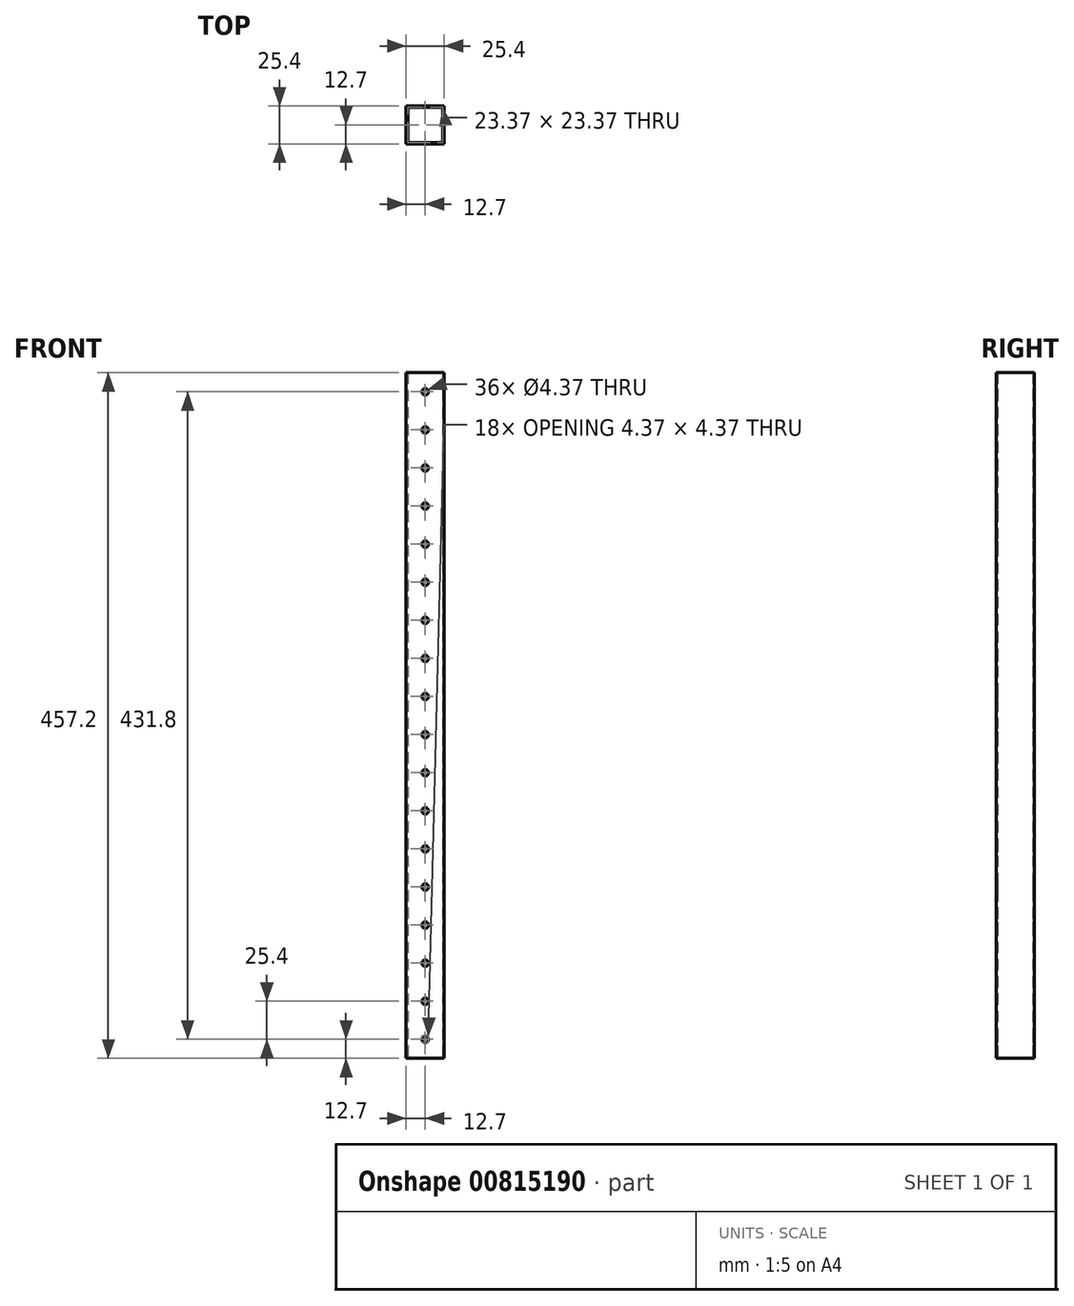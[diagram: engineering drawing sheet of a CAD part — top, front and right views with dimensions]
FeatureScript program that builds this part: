
annotation { "Feature Type Name" : "Feature", "Feature Type Description" : "" }
export const myFeature = defineFeature(function(context is Context, id is Id, definition is map)
    precondition{}
    {
        {
            var Q0;
            Q0=qCreatedBy(makeId("Top.planeOp"),FACE);
            var sketch = newSketch(context, id + "F0", { "sketchPlane" : qUnion([Q0])});
            skLineSegment(sketch, "E0.bottom", {"start": v(0, 0) * mm, "end": v(25.4, 0) * mm});
            skLineSegment(sketch, "E0.top", {"start": v(0, -25.4) * mm, "end": v(25.4, -25.4) * mm});
            skLineSegment(sketch, "E0.left", {"start": v(0, 0) * mm, "end": v(0, -25.4) * mm});
            skLineSegment(sketch, "E0.right", {"start": v(25.4, 0) * mm, "end": v(25.4, -25.4) * mm});
            skLineSegment(sketch, "E1.bottom", {"start": v(1.02, -1.02) * mm, "end": v(24.38, -1.02) * mm});
            skLineSegment(sketch, "E1.top", {"start": v(1.02, -24.38) * mm, "end": v(24.38, -24.38) * mm});
            skLineSegment(sketch, "E1.left", {"start": v(1.02, -1.02) * mm, "end": v(1.02, -24.38) * mm});
            skLineSegment(sketch, "E1.right", {"start": v(24.38, -1.02) * mm, "end": v(24.38, -24.38) * mm});
            skSolve(sketch);
        }
        {
            var Q0;
            Q0=makeQuery(id+"F0.imprint","IMPRINT",FACE,{"disambiguationData":[TD([[makeQuery(id+"F0.imprint","IMPRINT",EDGE,{"derivedFrom":sQuery(id+"F0.wireOp",EDGE,"E0.bottom")}),-1.0]])]});
            extrude(context, id + "F1", {"entities" : qUnion([Q0]), "depth" : 457.2 * mm, "offsetDistance" : 25.4 * mm});
        }
        {
            var Q0;
            Q0=makeQuery(id+"F1.opExtrude","SWEPT_FACE",FACE,{"disambiguationData":[OSD([sQuery(id+"F0.wireOp",EDGE,"E0.top")])]});
            var sketch = newSketch(context, id + "F2", { "sketchPlane" : qUnion([Q0])});
            skCircle(sketch, "E2", {"center": v(12.7, 12.7) * mm, "radius": 2.18 * mm});
            skCircle(sketch, "E3.0.1.0", {"center": v(12.7, 38.1) * mm, "radius": 2.18 * mm});
            skCircle(sketch, "E3.0.2.0", {"center": v(12.7, 63.5) * mm, "radius": 2.18 * mm});
            skCircle(sketch, "E3.0.3.0", {"center": v(12.7, 88.9) * mm, "radius": 2.18 * mm});
            skCircle(sketch, "E3.0.4.0", {"center": v(12.7, 114.3) * mm, "radius": 2.18 * mm});
            skCircle(sketch, "E3.0.5.0", {"center": v(12.7, 139.7) * mm, "radius": 2.18 * mm});
            skCircle(sketch, "E3.0.6.0", {"center": v(12.7, 165.1) * mm, "radius": 2.18 * mm});
            skCircle(sketch, "E3.0.7.0", {"center": v(12.7, 190.5) * mm, "radius": 2.18 * mm});
            skCircle(sketch, "E3.0.8.0", {"center": v(12.7, 215.9) * mm, "radius": 2.18 * mm});
            skCircle(sketch, "E3.0.9.0", {"center": v(12.7, 241.3) * mm, "radius": 2.18 * mm});
            skCircle(sketch, "E3.0.10.0", {"center": v(12.7, 266.7) * mm, "radius": 2.18 * mm});
            skCircle(sketch, "E3.0.11.0", {"center": v(12.7, 292.1) * mm, "radius": 2.18 * mm});
            skCircle(sketch, "E3.0.12.0", {"center": v(12.7, 317.5) * mm, "radius": 2.18 * mm});
            skCircle(sketch, "E3.0.13.0", {"center": v(12.7, 342.9) * mm, "radius": 2.18 * mm});
            skCircle(sketch, "E3.0.14.0", {"center": v(12.7, 368.3) * mm, "radius": 2.18 * mm});
            skCircle(sketch, "E3.0.15.0", {"center": v(12.7, 393.7) * mm, "radius": 2.18 * mm});
            skCircle(sketch, "E3.0.16.0", {"center": v(12.7, 419.1) * mm, "radius": 2.18 * mm});
            skCircle(sketch, "E3.0.17.0", {"center": v(12.7, 444.5) * mm, "radius": 2.18 * mm});
            skCircle(sketch, "E3.0.18.0", {"center": v(12.7, 469.9) * mm, "radius": 2.18 * mm});
            skCircle(sketch, "E3.0.19.0", {"center": v(12.7, 495.3) * mm, "radius": 2.18 * mm});
            skCircle(sketch, "E3.0.20.0", {"center": v(12.7, 520.7) * mm, "radius": 2.18 * mm});
            skCircle(sketch, "E3.0.21.0", {"center": v(12.7, 546.1) * mm, "radius": 2.18 * mm});
            skCircle(sketch, "E3.0.22.0", {"center": v(12.7, 571.5) * mm, "radius": 2.18 * mm});
            skCircle(sketch, "E3.0.23.0", {"center": v(12.7, 596.9) * mm, "radius": 2.18 * mm});
            skCircle(sketch, "E3.0.24.0", {"center": v(12.7, 622.3) * mm, "radius": 2.18 * mm});
            skLineSegment(sketch, "E3.direction1", {"start": v(12.7, 12.7) * mm, "end": v(38.1, 12.7) * mm, "construction": true});
            skLineSegment(sketch, "E3.direction2", {"start": v(12.7, 12.7) * mm, "end": v(12.7, 38.1) * mm, "construction": true});
            skSolve(sketch);
        }
        {
            var Q0;
            Q0=makeQuery(id+"F2.imprint","IMPRINT",FACE,{"disambiguationData":[TD([[makeQuery(id+"F2.imprint","IMPRINT",EDGE,{"derivedFrom":sQuery(id+"F2.wireOp",EDGE,"E2")}),1.0]])]});
            var Q1;
            Q1=makeQuery(id+"F2.imprint","IMPRINT",FACE,{"disambiguationData":[TD([[makeQuery(id+"F2.imprint","IMPRINT",EDGE,{"derivedFrom":sQuery(id+"F2.wireOp",EDGE,"E3.0.1.0")}),1.0]])]});
            var Q2;
            Q2=makeQuery(id+"F2.imprint","IMPRINT",FACE,{"disambiguationData":[TD([[makeQuery(id+"F2.imprint","IMPRINT",EDGE,{"derivedFrom":sQuery(id+"F2.wireOp",EDGE,"E3.0.9.0")}),1.0]])]});
            var Q3;
            Q3=makeQuery(id+"F2.imprint","IMPRINT",FACE,{"disambiguationData":[TD([[makeQuery(id+"F2.imprint","IMPRINT",EDGE,{"derivedFrom":sQuery(id+"F2.wireOp",EDGE,"E3.0.8.0")}),1.0]])]});
            var Q4;
            Q4=makeQuery(id+"F2.imprint","IMPRINT",FACE,{"disambiguationData":[TD([[makeQuery(id+"F2.imprint","IMPRINT",EDGE,{"derivedFrom":sQuery(id+"F2.wireOp",EDGE,"E3.0.7.0")}),1.0]])]});
            var Q5;
            Q5=makeQuery(id+"F2.imprint","IMPRINT",FACE,{"disambiguationData":[TD([[makeQuery(id+"F2.imprint","IMPRINT",EDGE,{"derivedFrom":sQuery(id+"F2.wireOp",EDGE,"E3.0.6.0")}),1.0]])]});
            var Q6;
            Q6=makeQuery(id+"F2.imprint","IMPRINT",FACE,{"disambiguationData":[TD([[makeQuery(id+"F2.imprint","IMPRINT",EDGE,{"derivedFrom":sQuery(id+"F2.wireOp",EDGE,"E3.0.5.0")}),1.0]])]});
            var Q7;
            Q7=makeQuery(id+"F2.imprint","IMPRINT",FACE,{"disambiguationData":[TD([[makeQuery(id+"F2.imprint","IMPRINT",EDGE,{"derivedFrom":sQuery(id+"F2.wireOp",EDGE,"E3.0.4.0")}),1.0]])]});
            var Q8;
            Q8=makeQuery(id+"F2.imprint","IMPRINT",FACE,{"disambiguationData":[TD([[makeQuery(id+"F2.imprint","IMPRINT",EDGE,{"derivedFrom":sQuery(id+"F2.wireOp",EDGE,"E3.0.3.0")}),1.0]])]});
            var Q9;
            Q9=makeQuery(id+"F2.imprint","IMPRINT",FACE,{"disambiguationData":[TD([[makeQuery(id+"F2.imprint","IMPRINT",EDGE,{"derivedFrom":sQuery(id+"F2.wireOp",EDGE,"E3.0.2.0")}),1.0]])]});
            var Q10;
            Q10=makeQuery(id+"F2.imprint","IMPRINT",FACE,{"disambiguationData":[TD([[makeQuery(id+"F2.imprint","IMPRINT",EDGE,{"derivedFrom":sQuery(id+"F2.wireOp",EDGE,"E3.0.10.0")}),1.0]])]});
            var Q11;
            Q11=makeQuery(id+"F2.imprint","IMPRINT",FACE,{"disambiguationData":[TD([[makeQuery(id+"F2.imprint","IMPRINT",EDGE,{"derivedFrom":sQuery(id+"F2.wireOp",EDGE,"E3.0.11.0")}),1.0]])]});
            var Q12;
            Q12=makeQuery(id+"F2.imprint","IMPRINT",FACE,{"disambiguationData":[TD([[makeQuery(id+"F2.imprint","IMPRINT",EDGE,{"derivedFrom":sQuery(id+"F2.wireOp",EDGE,"E3.0.12.0")}),1.0]])]});
            var Q13;
            Q13=makeQuery(id+"F2.imprint","IMPRINT",FACE,{"disambiguationData":[TD([[makeQuery(id+"F2.imprint","IMPRINT",EDGE,{"derivedFrom":sQuery(id+"F2.wireOp",EDGE,"E3.0.13.0")}),1.0]])]});
            var Q14;
            Q14=makeQuery(id+"F2.imprint","IMPRINT",FACE,{"disambiguationData":[TD([[makeQuery(id+"F2.imprint","IMPRINT",EDGE,{"derivedFrom":sQuery(id+"F2.wireOp",EDGE,"E3.0.14.0")}),1.0]])]});
            var Q15;
            Q15=makeQuery(id+"F2.imprint","IMPRINT",FACE,{"disambiguationData":[TD([[makeQuery(id+"F2.imprint","IMPRINT",EDGE,{"derivedFrom":sQuery(id+"F2.wireOp",EDGE,"E3.0.15.0")}),1.0]])]});
            var Q16;
            Q16=makeQuery(id+"F2.imprint","IMPRINT",FACE,{"disambiguationData":[TD([[makeQuery(id+"F2.imprint","IMPRINT",EDGE,{"derivedFrom":sQuery(id+"F2.wireOp",EDGE,"E3.0.16.0")}),1.0]])]});
            var Q17;
            Q17=makeQuery(id+"F2.imprint","IMPRINT",FACE,{"disambiguationData":[TD([[makeQuery(id+"F2.imprint","IMPRINT",EDGE,{"derivedFrom":sQuery(id+"F2.wireOp",EDGE,"E3.0.17.0")}),1.0]])]});
            var Q18;
            Q18=makeQuery(id+"F2.imprint","IMPRINT",FACE,{"disambiguationData":[TD([[makeQuery(id+"F2.imprint","IMPRINT",EDGE,{"derivedFrom":sQuery(id+"F2.wireOp",EDGE,"E3.0.18.0")}),1.0]])]});
            var Q19;
            Q19=makeQuery(id+"F2.imprint","IMPRINT",FACE,{"disambiguationData":[TD([[makeQuery(id+"F2.imprint","IMPRINT",EDGE,{"derivedFrom":sQuery(id+"F2.wireOp",EDGE,"E3.0.19.0")}),1.0]])]});
            var Q20;
            Q20=makeQuery(id+"F2.imprint","IMPRINT",FACE,{"disambiguationData":[TD([[makeQuery(id+"F2.imprint","IMPRINT",EDGE,{"derivedFrom":sQuery(id+"F2.wireOp",EDGE,"E3.0.20.0")}),1.0]])]});
            var Q21;
            Q21=makeQuery(id+"F2.imprint","IMPRINT",FACE,{"disambiguationData":[TD([[makeQuery(id+"F2.imprint","IMPRINT",EDGE,{"derivedFrom":sQuery(id+"F2.wireOp",EDGE,"E3.0.21.0")}),1.0]])]});
            var Q22;
            Q22=makeQuery(id+"F2.imprint","IMPRINT",FACE,{"disambiguationData":[TD([[makeQuery(id+"F2.imprint","IMPRINT",EDGE,{"derivedFrom":sQuery(id+"F2.wireOp",EDGE,"E3.0.22.0")}),1.0]])]});
            var Q23;
            Q23=makeQuery(id+"F2.imprint","IMPRINT",FACE,{"disambiguationData":[TD([[makeQuery(id+"F2.imprint","IMPRINT",EDGE,{"derivedFrom":sQuery(id+"F2.wireOp",EDGE,"E3.0.23.0")}),1.0]])]});
            var Q24;
            Q24=makeQuery(id+"F2.imprint","IMPRINT",FACE,{"disambiguationData":[TD([[makeQuery(id+"F2.imprint","IMPRINT",EDGE,{"derivedFrom":sQuery(id+"F2.wireOp",EDGE,"E3.0.24.0")}),1.0]])]});
            extrude(context, id + "F3", {"entities" : qUnion([Q0, Q1, Q2, Q3, Q4, Q5, Q6, Q7, Q8, Q9, Q10, Q11, Q12, Q13, Q14, Q15, Q16, Q17, Q18, Q19, Q20, Q21, Q22, Q23, Q24]), "operationType" : NewBodyOperationType.REMOVE, "oppositeDirection" : true, "depth" : 25.4 * mm, "offsetDistance" : 25.4 * mm});
        }
    });
